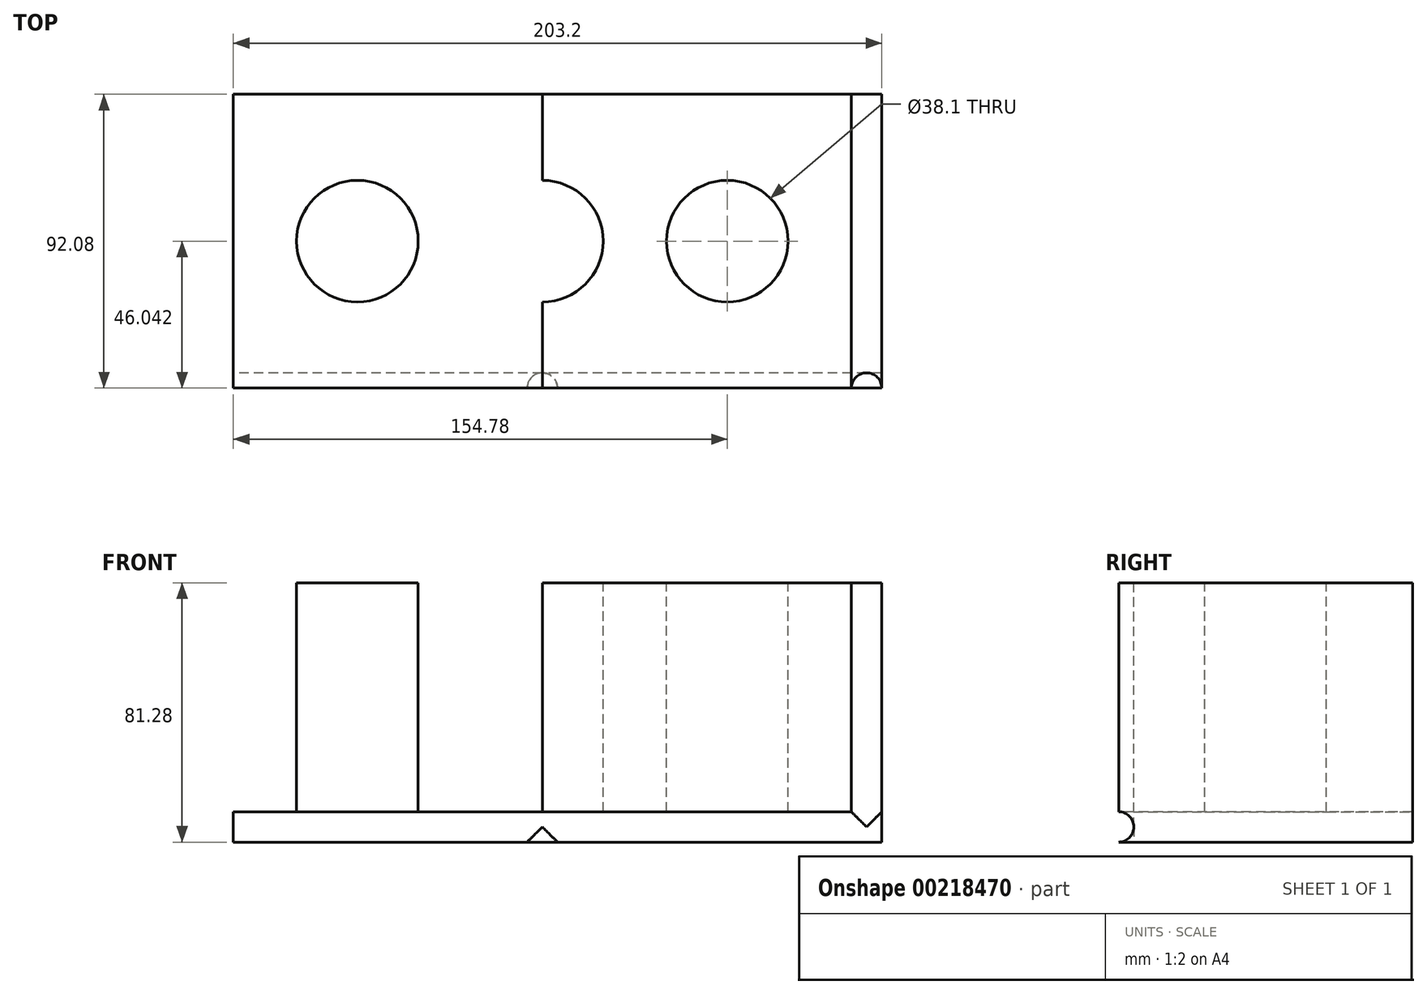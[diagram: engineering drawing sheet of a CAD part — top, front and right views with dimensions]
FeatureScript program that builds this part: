
annotation { "Feature Type Name" : "Feature", "Feature Type Description" : "" }
export const myFeature = defineFeature(function(context is Context, id is Id, definition is map)
    precondition{}
    {
        {
            var Q0;
            Q0=qCreatedBy(makeId("Front.planeOp"),FACE);
            var sketch = newSketch(context, id + "F0", { "sketchPlane" : qUnion([Q0])});
            skLineSegment(sketch, "E0", {"start": v(-46.45, 32.55) * mm, "end": v(-46.45, -39.2) * mm});
            skLineSegment(sketch, "E1", {"start": v(-46.45, -39.2) * mm, "end": v(147.22, -39.2) * mm});
            skLineSegment(sketch, "E2", {"start": v(147.22, -39.2) * mm, "end": v(147.22, 32.55) * mm});
            skLineSegment(sketch, "E3", {"start": v(147.22, 32.55) * mm, "end": v(-46.45, 32.55) * mm});
            skSolve(sketch);
        }
        {
            var Q0;
            Q0=makeQuery(id+"F0.imprint","IMPRINT",FACE,{"disambiguationData":[TD([[makeQuery(id+"F0.imprint","IMPRINT",EDGE,{"derivedFrom":sQuery(id+"F0.wireOp",EDGE,"E0")}),1.0]])]});
            extrude(context, id + "F1", {"entities" : qUnion([Q0]), "depth" : 92.07 * mm});
        }
        {
            var Q0;
            Q0=makeQuery(id+"F1.opExtrude","SWEPT_FACE",FACE,{"disambiguationData":[OSD([sQuery(id+"F0.wireOp",EDGE,"E3")])]});
            var sketch = newSketch(context, id + "F2", { "sketchPlane" : qUnion([Q0])});
            skCircle(sketch, "E4", {"center": v(50.39, -46.04) * mm, "radius": 19.05 * mm});
            skLineSegment(sketch, "E5.trimOffspring", {"start": v(69.44, -46.04) * mm, "end": v(147.22, -46.04) * mm});
            skPoint(sketch, "E6.start.orphan", {"position": v(-46.45, -46.04) * mm});
            skCircle(sketch, "E7", {"center": v(108.33, -46.04) * mm, "radius": 19.05 * mm});
            skLineSegment(sketch, "E8", {"start": v(50.39, 0) * mm, "end": v(50.39, -92.08) * mm});
            skCircle(sketch, "E9.MirrorC", {"center": v(-7.56, -46.04) * mm, "radius": 19.05 * mm});
            skSolve(sketch);
        }
        {
            var Q0;
            Q0=makeQuery(id+"F2.imprint","IMPRINT",FACE,{"disambiguationData":[TD([[makeQuery(id+"F2.imprint","IMPRINT",EDGE,{"derivedFrom":sQuery(id+"F2.wireOp",EDGE,"E9.MirrorC")}),-1.0]])]});
            var Q1;
            {var subQ0=sQuery(id+"F2.wireOp",EDGE,"E8");var subQ1=sQuery(id+"F2.wireOp",EDGE,"E4");var subQ2=makeQuery(id+"F2.imprint","INTERSECT",VERTEX,{"disambiguationData":[OD(0.0)],"derivedFrom":[subQ1,subQ0]});Q1=makeQuery(id+"F2.imprint","IMPRINT",FACE,{"disambiguationData":[TD([[makeQuery(id+"F2.imprint","IMPRINT",EDGE,{"disambiguationData":[TD([[subQ2,-1.0]])],"derivedFrom":subQ1}),1.0]])]});}
            var Q2;
            {var subQ0=sQuery(id+"F2.wireOp",EDGE,"E4");var subQ1=makeQuery(id+"F2.imprint","INTERSECT",VERTEX,{"derivedFrom":[subQ0,sQuery(id+"F2.wireOp",EDGE,"E5.trimOffspring")]});Q2=makeQuery(id+"F2.imprint","IMPRINT",FACE,{"disambiguationData":[TD([[makeQuery(id+"F2.imprint","IMPRINT",EDGE,{"disambiguationData":[TD([[subQ1,-1.0]])],"derivedFrom":subQ0}),1.0]])]});}
            var Q3;
            {var subQ0=sQuery(id+"F2.wireOp",EDGE,"E7");var subQ1=sQuery(id+"F2.wireOp",EDGE,"E5.trimOffspring");var subQ2=makeQuery(id+"F2.imprint","INTERSECT",VERTEX,{"disambiguationData":[OD(0.0)],"derivedFrom":[subQ1,subQ0]});Q3=makeQuery(id+"F2.imprint","IMPRINT",FACE,{"disambiguationData":[TD([[makeQuery(id+"F2.imprint","IMPRINT",EDGE,{"disambiguationData":[TD([[subQ2,-1.0]])],"derivedFrom":subQ1}),-1.0]])]});}
            var Q4;
            {var subQ0=sQuery(id+"F2.wireOp",EDGE,"E7");var subQ1=sQuery(id+"F2.wireOp",EDGE,"E5.trimOffspring");var subQ2=makeQuery(id+"F2.imprint","INTERSECT",VERTEX,{"disambiguationData":[OD(0.0)],"derivedFrom":[subQ1,subQ0]});Q4=makeQuery(id+"F2.imprint","IMPRINT",FACE,{"disambiguationData":[TD([[makeQuery(id+"F2.imprint","IMPRINT",EDGE,{"disambiguationData":[TD([[subQ2,-1.0]])],"derivedFrom":subQ1}),1.0]])]});}
            var Q5;
            Q5=makeQuery(id+"F1.opExtrude","SWEPT_FACE",FACE,{"disambiguationData":[OSD([sQuery(id+"F0.wireOp",EDGE,"E1")])]});
            extrude(context, id + "F3", {"entities" : qUnion([Q0, Q1, Q2, Q3, Q4]), "operationType" : NewBodyOperationType.REMOVE, "endBound" : BoundingType.UP_TO_SURFACE, "oppositeDirection" : true, "endBoundEntityFace" : qUnion([Q5]), "depth" : 25.4 * mm, "hasSecondDirection" : true, "secondDirectionOppositeDirection" : false, "secondDirectionDepth" : 25.4 * mm});
        }
        {
            var Q0;
            Q0=makeQuery(id+"F1.opExtrude","CAP_FACE",FACE,{"disambiguationData":[OSD([sQuery(id+"F0.wireOp",EDGE,"E0"),sQuery(id+"F0.wireOp",EDGE,"E1"),sQuery(id+"F0.wireOp",EDGE,"E2"),sQuery(id+"F0.wireOp",EDGE,"E3")])],"isStart":false});
            var sketch = newSketch(context, id + "F4", { "sketchPlane" : qUnion([Q0])});
            skLineSegment(sketch, "E10", {"start": v(147.22, 32.55) * mm, "end": v(156.75, 32.55) * mm});
            skLineSegment(sketch, "E11", {"start": v(156.75, 32.55) * mm, "end": v(156.75, -48.73) * mm});
            skLineSegment(sketch, "E12", {"start": v(156.75, -48.73) * mm, "end": v(-46.45, -48.73) * mm});
            skLineSegment(sketch, "E13", {"start": v(-46.45, -48.73) * mm, "end": v(-46.45, -39.2) * mm});
            skLineSegment(sketch, "E14", {"start": v(-46.45, -39.2) * mm, "end": v(147.22, -39.2) * mm});
            skLineSegment(sketch, "E15", {"start": v(147.22, -39.2) * mm, "end": v(147.22, 32.55) * mm});
            skSolve(sketch);
        }
        {
            var Q0;
            Q0 = qSketchRegion(id + "F4", true);
            extrude(context, id + "F5", {"entities" : qUnion([Q0]), "oppositeDirection" : true, "depth" : 92.07 * mm});
        }
        {
            var Q0;
            Q0=makeQuery(id+"F5.opExtrude","SWEPT_FACE",FACE,{"disambiguationData":[OSD([sQuery(id+"F4.wireOp",EDGE,"E10")])]});
            var sketch = newSketch(context, id + "F6", { "sketchPlane" : qUnion([Q0])});
            skCircle(sketch, "E16", {"center": v(151.99, -92.08) * mm, "radius": 4.76 * mm});
            skSolve(sketch);
        }
        {
            var Q0;
            Q0 = qSketchRegion(id + "F6", true);
            extrude(context, id + "F7", {"entities" : qUnion([Q0]), "operationType" : NewBodyOperationType.REMOVE, "oppositeDirection" : true, "depth" : 76.52 * mm});
        }
        {
            var Q0;
            Q0=makeQuery(id+"F5.opExtrude","SWEPT_FACE",FACE,{"disambiguationData":[OSD([sQuery(id+"F4.wireOp",EDGE,"E13")])]});
            var sketch = newSketch(context, id + "F8", { "sketchPlane" : qUnion([Q0])});
            skCircle(sketch, "E17", {"center": v(92.08, -43.97) * mm, "radius": 4.76 * mm});
            skSolve(sketch);
        }
        {
            var Q0;
            Q0 = qSketchRegion(id + "F8", true);
            extrude(context, id + "F9", {"entities" : qUnion([Q0]), "operationType" : NewBodyOperationType.REMOVE, "oppositeDirection" : true, "depth" : 203.2 * mm});
        }
        {
            var Q0;
            Q0=makeQuery(id+"F5.opExtrude","SWEPT_FACE",FACE,{"disambiguationData":[OSD([sQuery(id+"F4.wireOp",EDGE,"E12")])]});
            var sketch = newSketch(context, id + "F10", { "sketchPlane" : qUnion([Q0])});
            skCircle(sketch, "E18", {"center": v(50.39, 92.08) * mm, "radius": 4.76 * mm});
            skSolve(sketch);
        }
        {
            var Q0;
            Q0 = qSketchRegion(id + "F10", true);
            extrude(context, id + "F11", {"entities" : qUnion([Q0]), "operationType" : NewBodyOperationType.REMOVE, "oppositeDirection" : true, "depth" : 4.76 * mm});
        }
    });
